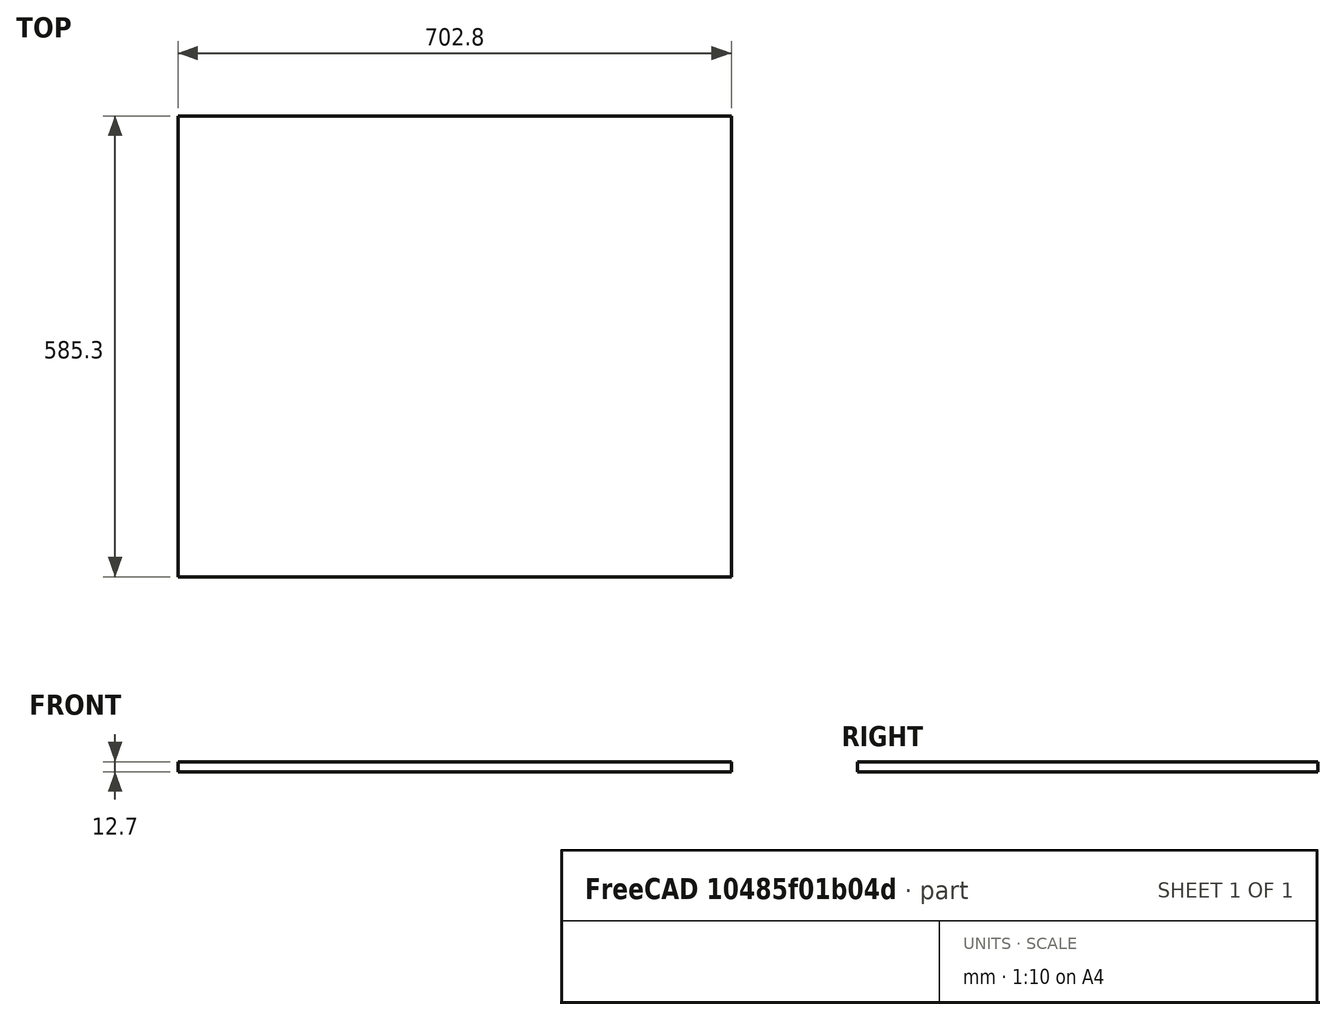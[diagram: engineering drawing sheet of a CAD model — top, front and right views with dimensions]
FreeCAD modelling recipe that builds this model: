
FCSTD DOCUMENT  (FreeCAD 0.19R24291 (Git))
Label: bottom
License: All rights reserved
LicenseURL: http://en.wikipedia.org/wiki/All_rights_reserved
objects: Sketcher::SketchObject×1, PartDesign::Pad×1, PartDesign::Body×1
note: 4 computed .brp shape members not serialized (recipe doc carries the construction recipe); baked Part::Feature solids carry a one-line shape summary decoded from their .brp

FEATURE [Sketcher::SketchObject] Sketch
  FullyConstrained = true
  MapMode = 5
  Support = -> [XY_Plane]
  expr: Constraints[9] = 704.8 - 2
  expr: Constraints[10] = 587.3 - 2
  sketch-geometry (4):
    g0: LineSegment StartX=0 StartY=0 StartZ=0 EndX=702.8 EndY=0 EndZ=0
    g1: LineSegment StartX=702.8 StartY=0 StartZ=0 EndX=702.8 EndY=585.3 EndZ=0
    g2: LineSegment StartX=702.8 StartY=585.3 StartZ=0 EndX=0 EndY=585.3 EndZ=0
    g3: LineSegment StartX=0 StartY=585.3 StartZ=0 EndX=0 EndY=0 EndZ=0
  constraints (11):
    c: Coincident(g0,g1)
    c: Coincident(g1,g2)
    c: Coincident(g2,g3)
    c: Coincident(g3,g0)
    c: Horizontal(g0)
    c: Horizontal(g2)
    c: Vertical(g1)
    c: Vertical(g3)
    c: Coincident(g0,g-1)
    c: DistanceX(g0,g0) = 702.8
    c: DistanceY(g3,g3) = 585.3
FEATURE [PartDesign::Pad] Pad
  Direction = (1,1,1)
  Length = 12.7
  Length2 = 100
  Profile = -> Sketch
  Type = 0
  expr: Length = 1 / 2 * 25.4
FEATURE [PartDesign::Body] Body
  Group = -> [Sketch,Pad]
  Origin = -> Origin
  Tip = -> Pad
